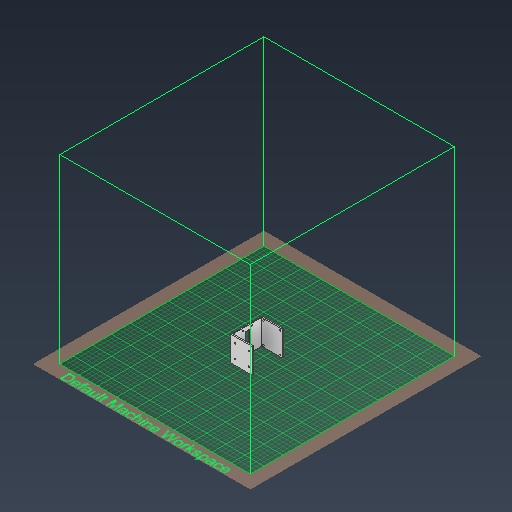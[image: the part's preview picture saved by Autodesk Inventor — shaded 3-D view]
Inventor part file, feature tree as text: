
AUTODESK INVENTOR PART (.ipt)
format: ipt  version: 2021 (Build 250183000, 183)  size: 398,336 bytes
history: native  units: mm
features: extrude x6, sketch x5, fillet x1
ambient origin geometry x8: Origin, YZ Plane, XZ Plane, XY Plane, X Axis, Y Axis, Z Axis, Center Point
bodies: Volumenkörper1 (feature_tree)
feature tree (12):
  extrude  "Extrusion1"  Depth=55.0mm
  extrude  "Extrusion2"  Depth=3.0mm
  extrude  "Extrusion3"  Depth=45.0mm TaperAngle=0.0deg
  extrude  "Extrusion4"  Depth=3.2mm
  sketch  "Skizze7"  dims[d44=3.2mm d47=3.2mm d50=45.0mm d51=0.0mm d52=3.2mm d53=3.2mm d63=3.2mm d65=3.2mm d66=45.0mm d67=0.0mm d69=6.0mm d70=4.0mm d71=4.0mm d72=6.0mm d73=4.0mm d74=4.0mm d75=4.0mm d76=4.0mm d84=15.0mm d86=9.5mm d87=9.5mm d88=15.0mm d89=15.0mm d90=7.5mm d91=7.5mm d92=15.0mm d93=3.2mm d95=5.0mm d96=3.2mm d97=5.0mm d99=3.2mm d100=5.0mm d101=20.0mm d102=3.2mm d103=5.0mm d104=20.0mm d105=10.0mm d106=0.0mm d107=36.0mm d108=10.0mm d111=10.0mm d112=10.0mm d113=10.0mm d114=0.0mm d115=2.0mm]
  extrude  "Extrusion5"  Depth=2.0mm
  extrude  "Extrusion6"  Depth=45.0mm TaperAngle=0.0deg
  fillet  "Rundung1"  Radius=3.2mm
  sketch  "Skizze2"  dims[d5=70.0mm d6=55.0mm]
  sketch  "Skizze3"  dims[d7=2.0mm d8=0.0mm d9=3.0mm]
  sketch  "Skizze5"  dims[d10=3.0mm d11=45.0mm d12=0.0mm]
  sketch  "Skizze6"  dims[d38=3.2mm d41=3.2mm]
